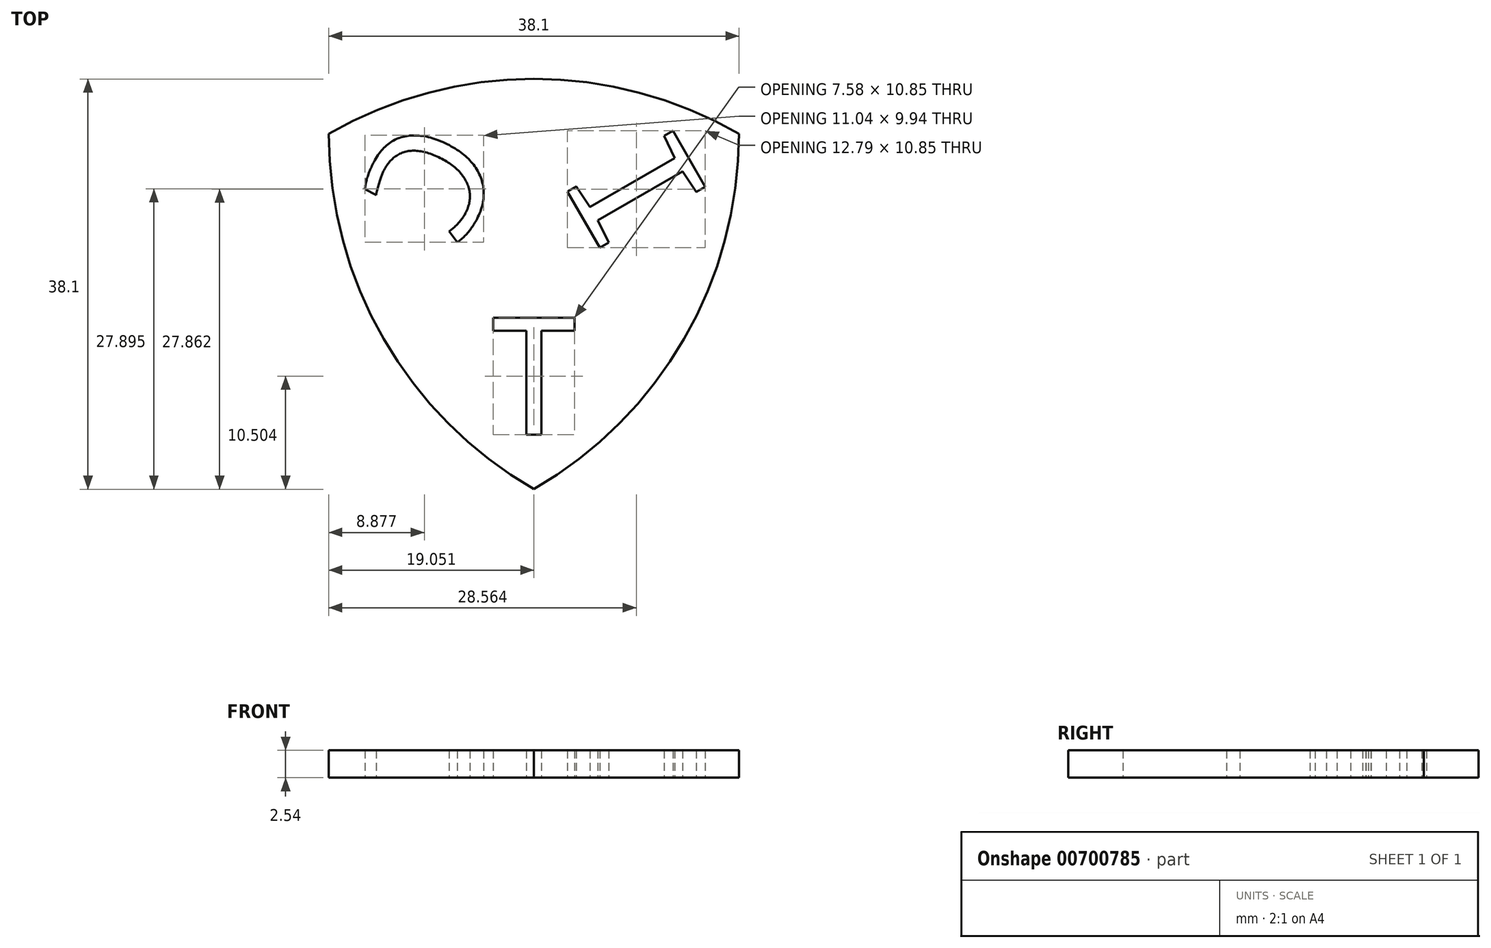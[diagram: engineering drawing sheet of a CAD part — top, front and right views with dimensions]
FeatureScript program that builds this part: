
annotation { "Feature Type Name" : "Feature", "Feature Type Description" : "" }
export const myFeature = defineFeature(function(context is Context, id is Id, definition is map)
    precondition{}
    {
        {
            var Q0;
            Q0=qCreatedBy(makeId("Top.planeOp"),FACE);
            var sketch = newSketch(context, id + "F0", { "sketchPlane" : qUnion([Q0])});
            skCircle(sketch, "E0", {"center": v(-38.1, 0) * mm, "radius": 38.1 * mm});
            skSolve(sketch);
        }
        {
            var Q0;
            Q0=qCreatedBy(makeId("Top.planeOp"),FACE);
            var sketch = newSketch(context, id + "F1", { "sketchPlane" : qUnion([Q0])});
            skCircle(sketch, "E1", {"center": v(0, 0) * mm, "radius": 38.1 * mm});
            skSolve(sketch);
        }
        {
            var Q0;
            Q0=qCreatedBy(makeId("Top.planeOp"),FACE);
            var sketch = newSketch(context, id + "F2", { "sketchPlane" : qUnion([Q0])});
            skCircle(sketch, "E2", {"center": v(-19.05, -33) * mm, "radius": 38.1 * mm});
            skSolve(sketch);
        }
        {
            var Q0;
            Q0=makeQuery(id+"F0.imprint","IMPRINT",FACE,{"disambiguationData":[TD([[makeQuery(id+"F0.imprint","IMPRINT",EDGE,{"derivedFrom":sQuery(id+"F0.wireOp",EDGE,"E0")}),1.0]])]});
            extrude(context, id + "F3", {"entities" : qUnion([Q0]), "depth" : 2.54 * mm, "offsetDistance" : 25.4 * mm});
        }
        {
            var Q0;
            Q0 = qSketchRegion(id + "F1", true);
            extrude(context, id + "F4", {"entities" : qUnion([Q0]), "depth" : 2.54 * mm, "offsetDistance" : 25.4 * mm});
        }
        {
            var Q0;
            Q0 = qSketchRegion(id + "F2", true);
            extrude(context, id + "F5", {"entities" : qUnion([Q0]), "depth" : 2.54 * mm, "offsetDistance" : 25.4 * mm});
        }
        {
            var Q0;
            Q0=makeQuery(id+"F3.opExtrude","SWEPT_BODY",BODY,{"disambiguationData":[OSD([sQuery(id+"F0.wireOp",EDGE,"E0")])]});
            var Q1;
            Q1=makeQuery(id+"F4.opExtrude","SWEPT_BODY",BODY,{"disambiguationData":[OSD([sQuery(id+"F1.wireOp",EDGE,"E1")])]});
            var Q2;
            Q2=makeQuery(id+"F5.opExtrude","SWEPT_BODY",BODY,{"disambiguationData":[OSD([sQuery(id+"F2.wireOp",EDGE,"E2")])]});
            booleanBodies(context, id + "F6", {"operationType" : BooleanOperationType.INTERSECTION, "tools" : qUnion([Q0, Q1, Q2])});
        }
        {
            var Q0;
            Q0=qCreatedBy(makeId("Top.planeOp"),FACE);
            var sketch = newSketch(context, id + "F7", { "sketchPlane" : qUnion([Q0])});
            skText(sketch, "E3", { "text": "I", "fontName": "DroidSansMono.ttf"});
            skText(sketch, "E4", { "text": "C", "fontName": "DroidSansMono.ttf"});
            skText(sketch, "E5", { "text": "T", "fontName": "DroidSansMono.ttf"});
            const initialGuessF7  = {"E3": [-0.0168, -0.00386, 0.5, -0.86603, 0.0114], "E4": [-0.0312, 0.00225, -0.46383, -0.88593, 0.01073], "E5": [-0.02436, -0.02792, 1, 0, 0.01094]};
            skSetInitialGuess(sketch, initialGuessF7);
            skSolve(sketch);
        }
        {
            var Q0;
            Q0 = qSketchRegion(id + "F7", true);
            extrude(context, id + "F8", {"entities" : qUnion([Q0]), "depth" : 2.54 * mm, "offsetDistance" : 25.4 * mm});
        }
        {
            var Q0;
            Q0=makeQuery(id+"F8.opExtrude","SWEPT_BODY",BODY,{"disambiguationData":[OSD([sQuery(id+"F7.wireOp",EDGE,"E5.sketch_text.stroke-0"),sQuery(id+"F7.wireOp",EDGE,"E5.sketch_text.stroke-1"),sQuery(id+"F7.wireOp",EDGE,"E5.sketch_text.stroke-2"),sQuery(id+"F7.wireOp",EDGE,"E5.sketch_text.stroke-3"),sQuery(id+"F7.wireOp",EDGE,"E5.sketch_text.stroke-4"),sQuery(id+"F7.wireOp",EDGE,"E5.sketch_text.stroke-5"),sQuery(id+"F7.wireOp",EDGE,"E5.sketch_text.stroke-6"),sQuery(id+"F7.wireOp",EDGE,"E5.sketch_text.stroke-7")])]});
            transform(context, id + "F9", {"entities" : qUnion([Q0]), "transformType" : TransformType.TRANSLATION_3D, "dx" : 0.76 * mm, "dy" : 0 * mm, "dz" : 0 * mm, "makeCopy" : false});
        }
        {
            var Q0;
            Q0=makeQuery(id+"F8.opExtrude","SWEPT_BODY",BODY,{"disambiguationData":[OSD([sQuery(id+"F7.wireOp",EDGE,"E5.sketch_text.stroke-0"),sQuery(id+"F7.wireOp",EDGE,"E5.sketch_text.stroke-1"),sQuery(id+"F7.wireOp",EDGE,"E5.sketch_text.stroke-2"),sQuery(id+"F7.wireOp",EDGE,"E5.sketch_text.stroke-3"),sQuery(id+"F7.wireOp",EDGE,"E5.sketch_text.stroke-4"),sQuery(id+"F7.wireOp",EDGE,"E5.sketch_text.stroke-5"),sQuery(id+"F7.wireOp",EDGE,"E5.sketch_text.stroke-6"),sQuery(id+"F7.wireOp",EDGE,"E5.sketch_text.stroke-7")])]});
            var Q1;
            Q1=makeQuery(id+"F8.opExtrude","SWEPT_BODY",BODY,{"disambiguationData":[OSD([sQuery(id+"F7.wireOp",EDGE,"E4.sketch_text.stroke-0"),sQuery(id+"F7.wireOp",EDGE,"E4.sketch_text.stroke-1"),sQuery(id+"F7.wireOp",EDGE,"E4.sketch_text.stroke-2"),sQuery(id+"F7.wireOp",EDGE,"E4.sketch_text.stroke-3"),sQuery(id+"F7.wireOp",EDGE,"E4.sketch_text.stroke-4"),sQuery(id+"F7.wireOp",EDGE,"E4.sketch_text.stroke-5"),sQuery(id+"F7.wireOp",EDGE,"E4.sketch_text.stroke-6"),sQuery(id+"F7.wireOp",EDGE,"E4.sketch_text.stroke-7"),sQuery(id+"F7.wireOp",EDGE,"E4.sketch_text.stroke-8"),sQuery(id+"F7.wireOp",EDGE,"E4.sketch_text.stroke-9"),sQuery(id+"F7.wireOp",EDGE,"E4.sketch_text.stroke-10"),sQuery(id+"F7.wireOp",EDGE,"E4.sketch_text.stroke-11"),sQuery(id+"F7.wireOp",EDGE,"E4.sketch_text.stroke-12"),sQuery(id+"F7.wireOp",EDGE,"E4.sketch_text.stroke-13")])]});
            var Q2;
            Q2=makeQuery(id+"F8.opExtrude","SWEPT_BODY",BODY,{"disambiguationData":[OSD([sQuery(id+"F7.wireOp",EDGE,"E3.sketch_text.stroke-0"),sQuery(id+"F7.wireOp",EDGE,"E3.sketch_text.stroke-1"),sQuery(id+"F7.wireOp",EDGE,"E3.sketch_text.stroke-2"),sQuery(id+"F7.wireOp",EDGE,"E3.sketch_text.stroke-3"),sQuery(id+"F7.wireOp",EDGE,"E3.sketch_text.stroke-4"),sQuery(id+"F7.wireOp",EDGE,"E3.sketch_text.stroke-5"),sQuery(id+"F7.wireOp",EDGE,"E3.sketch_text.stroke-6"),sQuery(id+"F7.wireOp",EDGE,"E3.sketch_text.stroke-7"),sQuery(id+"F7.wireOp",EDGE,"E3.sketch_text.stroke-8"),sQuery(id+"F7.wireOp",EDGE,"E3.sketch_text.stroke-9"),sQuery(id+"F7.wireOp",EDGE,"E3.sketch_text.stroke-10"),sQuery(id+"F7.wireOp",EDGE,"E3.sketch_text.stroke-11")])]});
            var Q3;
            Q3=makeQuery(id+"F6.opBoolean","INTERSECT",BODY,{"derivedFrom":[makeQuery(id+"F3.opExtrude","SWEPT_BODY",BODY,{"disambiguationData":[OSD([sQuery(id+"F0.wireOp",EDGE,"E0")])]}),makeQuery(id+"F4.opExtrude","SWEPT_BODY",BODY,{"disambiguationData":[OSD([sQuery(id+"F1.wireOp",EDGE,"E1")])]}),makeQuery(id+"F5.opExtrude","SWEPT_BODY",BODY,{"disambiguationData":[OSD([sQuery(id+"F2.wireOp",EDGE,"E2")])]})]});
            booleanBodies(context, id + "F10", {"operationType" : BooleanOperationType.SUBTRACTION, "tools" : qUnion([Q0, Q1, Q2]), "targets" : qUnion([Q3])});
        }
    });
